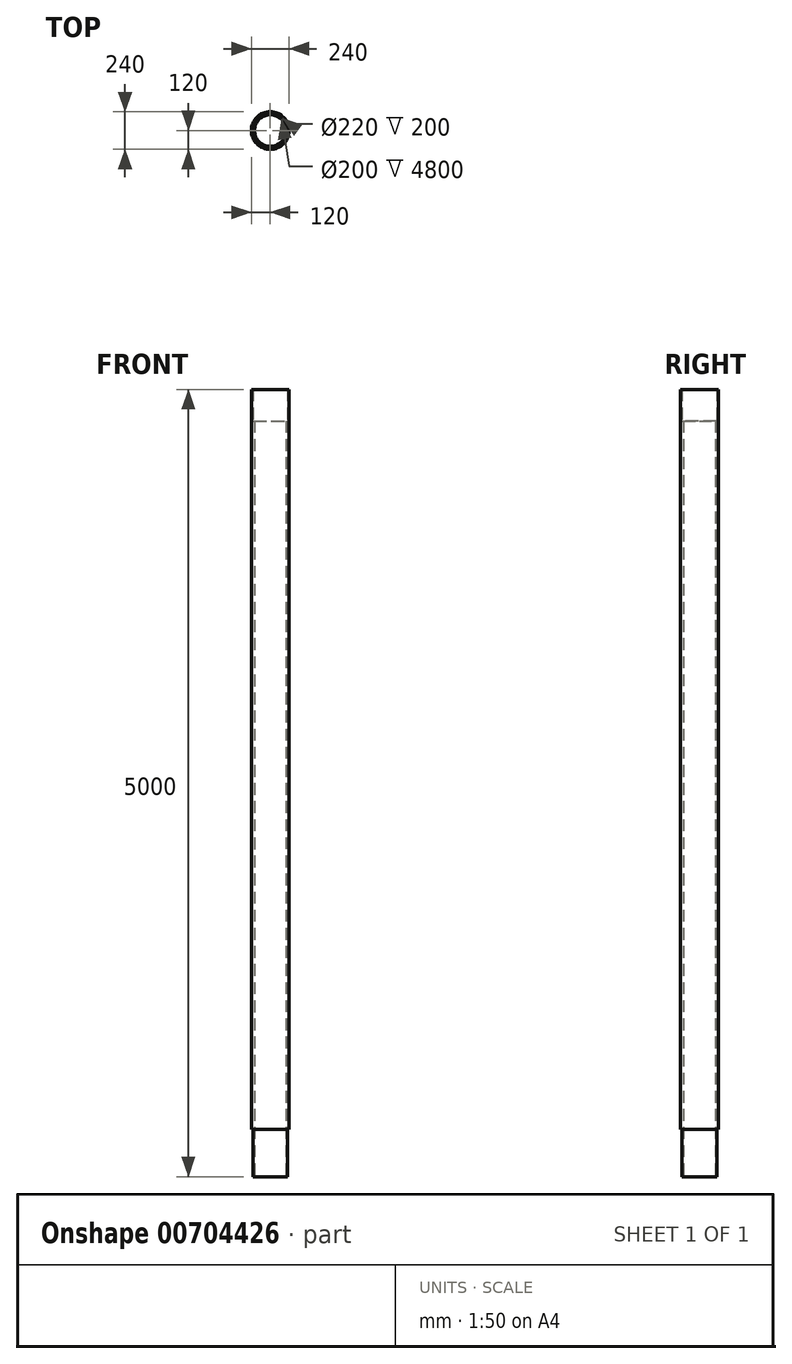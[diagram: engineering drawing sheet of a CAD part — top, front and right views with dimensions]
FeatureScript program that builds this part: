
annotation { "Feature Type Name" : "Feature", "Feature Type Description" : "" }
export const myFeature = defineFeature(function(context is Context, id is Id, definition is map)
    precondition{}
    {
        {
            var Q0;
            Q0=qCreatedBy(makeId("Front.planeOp"),FACE);
            var sketch = newSketch(context, id + "F0", { "sketchPlane" : qUnion([Q0])});
            skLineSegment(sketch, "E0", {"start": v(-100, -2499.78) * mm, "end": v(-100, 2300.22) * mm});
            skLineSegment(sketch, "E1", {"start": v(0, -2499.78) * mm, "end": v(0, 2500.22) * mm, "construction": true});
            skLineSegment(sketch, "E2", {"start": v(-120, -2199.78) * mm, "end": v(-120, 2500.22) * mm});
            skLineSegment(sketch, "E3", {"start": v(-64.78, -2499.78) * mm, "end": v(-64.78, -2199.78) * mm, "construction": true});
            skLineSegment(sketch, "E4", {"start": v(-64.78, -2199.78) * mm, "end": v(-266.23, -2199.78) * mm, "construction": true});
            skLineSegment(sketch, "E5", {"start": v(-110, -2499.78) * mm, "end": v(-110, -2199.78) * mm});
            skLineSegment(sketch, "E6", {"start": v(-120, -2199.78) * mm, "end": v(-110, -2199.78) * mm});
            skLineSegment(sketch, "E7", {"start": v(-110, 2500.22) * mm, "end": v(-110, 2300.22) * mm});
            skLineSegment(sketch, "E8", {"start": v(-110, 2300.22) * mm, "end": v(-100, 2300.22) * mm});
            skLineSegment(sketch, "E9", {"start": v(-110, 2500.22) * mm, "end": v(-120, 2500.22) * mm});
            skLineSegment(sketch, "E10", {"start": v(-100, -2499.78) * mm, "end": v(-110, -2499.78) * mm});
            skSolve(sketch);
        }
        {
            var Q0;
            Q0=makeQuery(id+"F0.imprint","IMPRINT",FACE,{"disambiguationData":[TD([[makeQuery(id+"F0.imprint","IMPRINT",EDGE,{"derivedFrom":sQuery(id+"F0.wireOp",EDGE,"E0")}),1.0]])]});
            var Q1;
            Q1=sQuery(id+"F0.wireOp",EDGE,"E1");
            revolve(context, id + "F1", {"surfaceOperationType" : NewSurfaceOperationType.NEW, "entities" : qUnion([Q0]), "axis" : qUnion([Q1]), "revolveType" : RevolveType.FULL});
        }
    });
